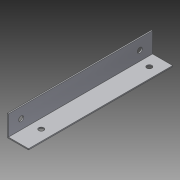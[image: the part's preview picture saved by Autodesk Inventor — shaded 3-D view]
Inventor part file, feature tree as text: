
AUTODESK INVENTOR PART (.ipt)
format: ipt  version: 2014 SP1 (Build 180222100, 222)  size: 100,352 bytes
history: native  units: in
note: dims shown in document units (in); Inventor stores cm internally (conversion verified against a paired STEP export)
features: extrude x3, sketch x3, reference x2
ambient origin geometry x8: Origin, YZ Plane, XZ Plane, XY Plane, X Axis, Y Axis, Z Axis, Center Point
bodies: Solid1 (feature_tree)
feature tree (8):
  extrude  "Extrusion1"  Depth=0.0312in
  extrude  "Extrusion2"  Depth=4.25in
  extrude  "Extrusion3"  Depth=0.625in
  sketch  "Sketch1"  dims[d0=0.625in d1=0.0312in]
  sketch  "Sketch2"  dims[d2=4.25in d3=0.0in d4=0.15in]
  sketch  "Sketch3"  dims[d6=0.6875in d7=0.375in d8=1.0in d9=0.0in d11=0.15in d12=0.375in d13=0.375in d14=1.0in d15=0.0in d16=0.625in d17=0.375in]
  reference  "Reference1"
  reference  "Reference2"
